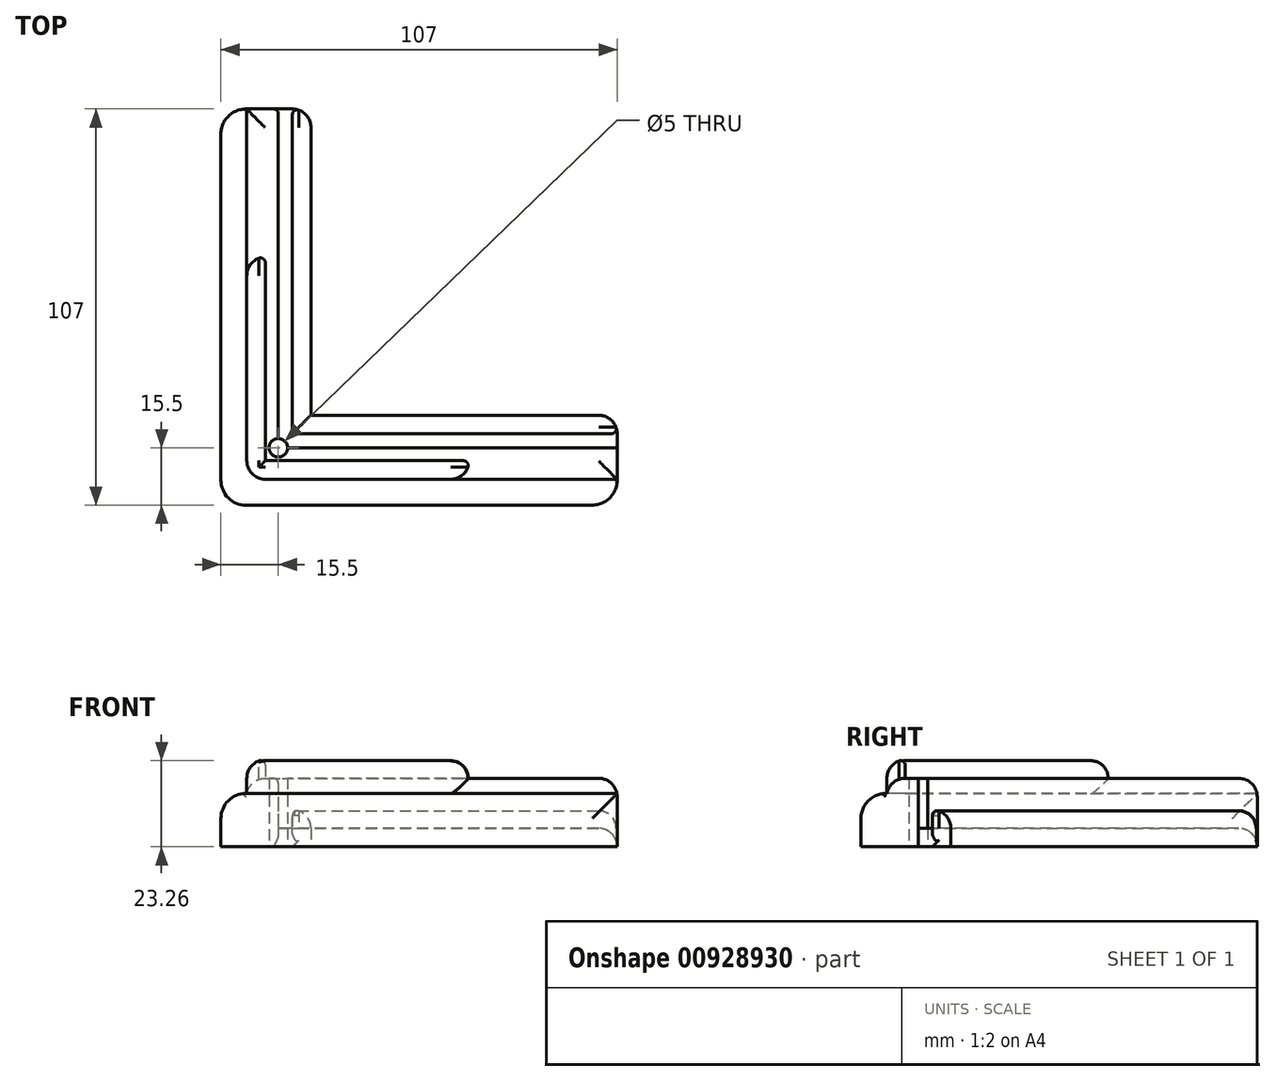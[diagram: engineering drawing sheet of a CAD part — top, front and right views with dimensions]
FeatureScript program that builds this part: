
annotation { "Feature Type Name" : "Feature", "Feature Type Description" : "" }
export const myFeature = defineFeature(function(context is Context, id is Id, definition is map)
    precondition{}
    {
        {
            var Q0;
            Q0=qCreatedBy(makeId("Top.planeOp"),FACE);
            var sketch = newSketch(context, id + "F0", { "sketchPlane" : qUnion([Q0])});
            skLineSegment(sketch, "E0", {"start": v(0, 0) * mm, "end": v(0, 91.5) * mm});
            skLineSegment(sketch, "E1", {"start": v(0, 91.5) * mm, "end": v(3.8, 91.5) * mm});
            skLineSegment(sketch, "E2", {"start": v(3.8, 91.5) * mm, "end": v(3.8, 3.8) * mm});
            skLineSegment(sketch, "E3", {"start": v(3.8, 3.8) * mm, "end": v(91.5, 3.8) * mm});
            skLineSegment(sketch, "E4", {"start": v(91.5, 3.8) * mm, "end": v(91.5, 0) * mm});
            skLineSegment(sketch, "E5", {"start": v(91.5, 0) * mm, "end": v(0, 0) * mm});
            skLineSegment(sketch, "E6", {"start": v(3.8, 91.5) * mm, "end": v(8.8, 91.5) * mm});
            skLineSegment(sketch, "E7", {"start": v(8.8, 91.5) * mm, "end": v(8.8, 8.8) * mm});
            skLineSegment(sketch, "E8", {"start": v(8.8, 8.8) * mm, "end": v(91.5, 8.8) * mm});
            skLineSegment(sketch, "E9", {"start": v(91.5, 8.8) * mm, "end": v(91.5, 3.8) * mm});
            skLineSegment(sketch, "E10", {"start": v(91.5, 0) * mm, "end": v(91.5, -3.5) * mm});
            skLineSegment(sketch, "E11", {"start": v(-3.5, 91.5) * mm, "end": v(0, 91.5) * mm});
            skLineSegment(sketch, "E12", {"start": v(91.5, -3.5) * mm, "end": v(91.5, -8.5) * mm});
            skLineSegment(sketch, "E13", {"start": v(91.5, -8.5) * mm, "end": v(-8.5, -8.5) * mm});
            skLineSegment(sketch, "E14", {"start": v(-8.5, -8.5) * mm, "end": v(-8.5, 91.5) * mm});
            skLineSegment(sketch, "E15", {"start": v(-8.5, 91.5) * mm, "end": v(-3.5, 91.5) * mm});
            skLineSegment(sketch, "E16", {"start": v(-8.5, 91.5) * mm, "end": v(-15.5, 91.5) * mm});
            skLineSegment(sketch, "E17", {"start": v(-15.5, 91.5) * mm, "end": v(-15.5, -15.5) * mm});
            skLineSegment(sketch, "E18", {"start": v(-15.5, -15.5) * mm, "end": v(91.5, -15.5) * mm});
            skLineSegment(sketch, "E19", {"start": v(91.5, -15.5) * mm, "end": v(91.5, -8.5) * mm});
            skSolve(sketch);
        }
        {
            var Q0;
            Q0=makeQuery(id+"F0.imprint","IMPRINT",FACE,{"disambiguationData":[TD([[makeQuery(id+"F0.imprint","IMPRINT",EDGE,{"derivedFrom":sQuery(id+"F0.wireOp",EDGE,"E2")}),1.0]])]});
            var Q1;
            Q1=makeQuery(id+"F0.imprint","IMPRINT",FACE,{"disambiguationData":[TD([[makeQuery(id+"F0.imprint","IMPRINT",EDGE,{"derivedFrom":sQuery(id+"F0.wireOp",EDGE,"E0")}),-1.0]])]});
            var Q2;
            Q2=makeQuery(id+"F0.imprint","IMPRINT",FACE,{"disambiguationData":[TD([[makeQuery(id+"F0.imprint","IMPRINT",EDGE,{"derivedFrom":sQuery(id+"F0.wireOp",EDGE,"E0")}),1.0]])]});
            var Q3;
            Q3=makeQuery(id+"F0.imprint","IMPRINT",FACE,{"disambiguationData":[TD([[makeQuery(id+"F0.imprint","IMPRINT",EDGE,{"derivedFrom":sQuery(id+"F0.wireOp",EDGE,"OfsXpkOs-3l8G-isar-b0VL-Z3l6h46DC14G")}),1.0]])]});
            extrude(context, id + "F1", {"entities" : qUnion([Q0, Q1, Q2, Q3]), "depth" : 5 * mm, "offsetDistance" : 25 * mm});
        }
        {
            var Q0;
            Q0=makeQuery(id+"F1.opExtrude","CAP_FACE",FACE,{"disambiguationData":[OSD([sQuery(id+"F0.wireOp",EDGE,"E1"),sQuery(id+"F0.wireOp",EDGE,"E4"),sQuery(id+"F0.wireOp",EDGE,"E6"),sQuery(id+"F0.wireOp",EDGE,"E7"),sQuery(id+"F0.wireOp",EDGE,"E8"),sQuery(id+"F0.wireOp",EDGE,"E9"),sQuery(id+"F0.wireOp",EDGE,"E10"),sQuery(id+"F0.wireOp",EDGE,"E11"),sQuery(id+"F0.wireOp",EDGE,"E12"),sQuery(id+"F0.wireOp",EDGE,"E13"),sQuery(id+"F0.wireOp",EDGE,"E14"),sQuery(id+"F0.wireOp",EDGE,"E15")])],"isStart":false});
            var sketch = newSketch(context, id + "F2", { "sketchPlane" : qUnion([Q0])});
            skLineSegment(sketch, "E20", {"start": v(0, 0) * mm, "end": v(0, 91.5) * mm});
            skLineSegment(sketch, "E21", {"start": v(0, 91.5) * mm, "end": v(3.8, 91.5) * mm});
            skLineSegment(sketch, "E22", {"start": v(3.8, 91.5) * mm, "end": v(3.8, 3.8) * mm});
            skLineSegment(sketch, "E23", {"start": v(3.8, 3.8) * mm, "end": v(91.5, 3.8) * mm});
            skLineSegment(sketch, "E24", {"start": v(91.5, 3.8) * mm, "end": v(91.5, 0) * mm});
            skLineSegment(sketch, "E25", {"start": v(91.5, 0) * mm, "end": v(0, 0) * mm});
            skLineSegment(sketch, "E26", {"start": v(3.8, 91.5) * mm, "end": v(8.8, 91.5) * mm});
            skLineSegment(sketch, "E27", {"start": v(8.8, 91.5) * mm, "end": v(8.8, 8.8) * mm});
            skLineSegment(sketch, "E28", {"start": v(8.8, 8.8) * mm, "end": v(91.5, 8.8) * mm});
            skLineSegment(sketch, "E29", {"start": v(91.5, 8.8) * mm, "end": v(91.5, 3.8) * mm});
            skLineSegment(sketch, "E30", {"start": v(91.5, 0) * mm, "end": v(91.5, -3.5) * mm});
            skLineSegment(sketch, "E31", {"start": v(-3.5, -3.5) * mm, "end": v(-3.5, 91.5) * mm});
            skLineSegment(sketch, "E32", {"start": v(-3.5, 91.5) * mm, "end": v(0, 91.5) * mm});
            skLineSegment(sketch, "E33", {"start": v(91.5, -3.5) * mm, "end": v(91.5, -8.5) * mm});
            skLineSegment(sketch, "E34", {"start": v(91.5, -8.5) * mm, "end": v(-8.5, -8.5) * mm});
            skLineSegment(sketch, "E35", {"start": v(-8.5, -8.5) * mm, "end": v(-8.5, 91.5) * mm});
            skLineSegment(sketch, "E36", {"start": v(-8.5, 91.5) * mm, "end": v(-3.5, 91.5) * mm});
            skLineSegment(sketch, "E37", {"start": v(-3.5, -3.5) * mm, "end": v(91.5, -3.5) * mm});
            skSolve(sketch);
        }
        {
            var Q0;
            Q0=makeQuery(id+"F2.imprint","IMPRINT",FACE,{"disambiguationData":[TD([[makeQuery(id+"F2.imprint","IMPRINT",EDGE,{"derivedFrom":sQuery(id+"F2.wireOp",EDGE,"E22")}),1.0]])]});
            var Q1;
            Q1=makeQuery(id+"F2.imprint","IMPRINT",FACE,{"disambiguationData":[TD([[makeQuery(id+"F2.imprint","IMPRINT",EDGE,{"derivedFrom":sQuery(id+"F2.wireOp",EDGE,"E20")}),1.0]])]});
            var Q2;
            Q2=makeQuery(id+"F2.imprint","IMPRINT",FACE,{"disambiguationData":[TD([[makeQuery(id+"F2.imprint","IMPRINT",EDGE,{"derivedFrom":sQuery(id+"F2.wireOp",EDGE,"E31")}),1.0]])]});
            extrude(context, id + "F3", {"entities" : qUnion([Q0, Q1, Q2]), "operationType" : NewBodyOperationType.ADD, "depth" : 5 * mm, "offsetDistance" : 25 * mm});
        }
        {
            var Q0;
            Q0=makeQuery(id+"F3.opExtrude","CAP_FACE",FACE,{"disambiguationData":[OSD([sQuery(id+"F2.wireOp",EDGE,"E20"),sQuery(id+"F2.wireOp",EDGE,"E25"),sQuery(id+"F2.wireOp",EDGE,"E30"),sQuery(id+"F2.wireOp",EDGE,"E32"),sQuery(id+"F2.wireOp",EDGE,"E33"),sQuery(id+"F2.wireOp",EDGE,"E34"),sQuery(id+"F2.wireOp",EDGE,"E35"),sQuery(id+"F2.wireOp",EDGE,"E36")])],"isStart":false});
            var sketch = newSketch(context, id + "F4", { "sketchPlane" : qUnion([Q0])});
            skLineSegment(sketch, "E38", {"start": v(0, 0) * mm, "end": v(0, 91.5) * mm});
            skLineSegment(sketch, "E39", {"start": v(0, 91.5) * mm, "end": v(3.8, 91.5) * mm});
            skLineSegment(sketch, "E40", {"start": v(3.8, 91.5) * mm, "end": v(3.8, 3.8) * mm});
            skLineSegment(sketch, "E41", {"start": v(3.8, 3.8) * mm, "end": v(91.5, 3.8) * mm});
            skLineSegment(sketch, "E42", {"start": v(91.5, 3.8) * mm, "end": v(91.5, 0) * mm});
            skLineSegment(sketch, "E43", {"start": v(91.5, 0) * mm, "end": v(0, 0) * mm});
            skLineSegment(sketch, "E44", {"start": v(3.8, 91.5) * mm, "end": v(8.8, 91.5) * mm});
            skLineSegment(sketch, "E45", {"start": v(8.8, 91.5) * mm, "end": v(8.8, 8.8) * mm});
            skLineSegment(sketch, "E46", {"start": v(8.8, 8.8) * mm, "end": v(91.5, 8.8) * mm});
            skLineSegment(sketch, "E47", {"start": v(91.5, 8.8) * mm, "end": v(91.5, 3.8) * mm});
            skLineSegment(sketch, "E48", {"start": v(91.5, 0) * mm, "end": v(91.5, -3.5) * mm});
            skLineSegment(sketch, "E49", {"start": v(-3.5, -3.5) * mm, "end": v(-3.5, 91.5) * mm});
            skLineSegment(sketch, "E50", {"start": v(-3.5, 91.5) * mm, "end": v(0, 91.5) * mm});
            skLineSegment(sketch, "E51", {"start": v(91.5, -3.5) * mm, "end": v(91.5, -8.5) * mm});
            skLineSegment(sketch, "E52", {"start": v(91.5, -8.5) * mm, "end": v(-8.5, -8.5) * mm});
            skLineSegment(sketch, "E53", {"start": v(-8.5, -8.5) * mm, "end": v(-8.5, 91.5) * mm});
            skLineSegment(sketch, "E54", {"start": v(-8.5, 91.5) * mm, "end": v(-3.5, 91.5) * mm});
            skLineSegment(sketch, "E55", {"start": v(-3.5, -3.5) * mm, "end": v(91.5, -3.5) * mm});
            skSolve(sketch);
        }
        {
            var Q0;
            Q0=makeQuery(id+"F4.imprint","IMPRINT",FACE,{"disambiguationData":[TD([[makeQuery(id+"F4.imprint","IMPRINT",EDGE,{"derivedFrom":sQuery(id+"F4.wireOp",EDGE,"E38")}),1.0]])]});
            var Q1;
            Q1=makeQuery(id+"F4.imprint","IMPRINT",FACE,{"disambiguationData":[TD([[makeQuery(id+"F4.imprint","IMPRINT",EDGE,{"derivedFrom":sQuery(id+"F4.wireOp",EDGE,"E49")}),1.0]])]});
            extrude(context, id + "F5", {"entities" : qUnion([Q0, Q1]), "operationType" : NewBodyOperationType.ADD, "depth" : 8.5 * mm, "offsetDistance" : 25 * mm});
        }
        {
            var Q0;
            Q0=makeQuery(id+"F5.opExtrude","CAP_FACE",FACE,{"disambiguationData":[OSD([sQuery(id+"F4.wireOp",EDGE,"E38"),sQuery(id+"F4.wireOp",EDGE,"E43"),sQuery(id+"F4.wireOp",EDGE,"E48"),sQuery(id+"F4.wireOp",EDGE,"E50"),sQuery(id+"F4.wireOp",EDGE,"E51"),sQuery(id+"F4.wireOp",EDGE,"E52"),sQuery(id+"F4.wireOp",EDGE,"E53"),sQuery(id+"F4.wireOp",EDGE,"E54")])],"isStart":false});
            var sketch = newSketch(context, id + "F6", { "sketchPlane" : qUnion([Q0])});
            skLineSegment(sketch, "E56", {"start": v(0, 0) * mm, "end": v(0, 51.5) * mm});
            skLineSegment(sketch, "E57", {"start": v(0, 51.5) * mm, "end": v(3.8, 51.5) * mm});
            skLineSegment(sketch, "E58", {"start": v(3.8, 51.5) * mm, "end": v(3.8, 3.8) * mm});
            skLineSegment(sketch, "E59", {"start": v(3.8, 3.8) * mm, "end": v(51.5, 3.8) * mm});
            skLineSegment(sketch, "E60", {"start": v(51.5, 3.8) * mm, "end": v(51.5, 0) * mm});
            skLineSegment(sketch, "E61", {"start": v(51.5, 0) * mm, "end": v(0, 0) * mm});
            skLineSegment(sketch, "E62", {"start": v(3.8, 51.5) * mm, "end": v(8.8, 51.5) * mm});
            skLineSegment(sketch, "E63", {"start": v(8.8, 51.5) * mm, "end": v(8.8, 8.8) * mm});
            skLineSegment(sketch, "E64", {"start": v(8.8, 8.8) * mm, "end": v(51.5, 8.8) * mm});
            skLineSegment(sketch, "E65", {"start": v(51.5, 8.8) * mm, "end": v(51.5, 3.8) * mm});
            skLineSegment(sketch, "E66", {"start": v(51.5, 0) * mm, "end": v(51.5, -3.5) * mm});
            skLineSegment(sketch, "E67", {"start": v(-3.5, -3.5) * mm, "end": v(-3.5, 51.5) * mm});
            skLineSegment(sketch, "E68", {"start": v(-3.5, 51.5) * mm, "end": v(0, 51.5) * mm});
            skLineSegment(sketch, "E69", {"start": v(51.5, -3.5) * mm, "end": v(51.5, -8.5) * mm});
            skLineSegment(sketch, "E70", {"start": v(51.5, -8.5) * mm, "end": v(-8.5, -8.5) * mm});
            skLineSegment(sketch, "E71", {"start": v(-8.5, -8.5) * mm, "end": v(-8.5, 51.5) * mm});
            skLineSegment(sketch, "E72", {"start": v(-8.5, 51.5) * mm, "end": v(-3.5, 51.5) * mm});
            skLineSegment(sketch, "E73", {"start": v(-3.5, -3.5) * mm, "end": v(51.5, -3.5) * mm});
            skSolve(sketch);
        }
        {
            var Q0;
            Q0=makeQuery(id+"F6.imprint","IMPRINT",FACE,{"disambiguationData":[TD([[makeQuery(id+"F6.imprint","IMPRINT",EDGE,{"derivedFrom":sQuery(id+"F6.wireOp",EDGE,"E67")}),1.0]])]});
            extrude(context, id + "F7", {"entities" : qUnion([Q0]), "operationType" : NewBodyOperationType.ADD, "depth" : 5 * mm, "offsetDistance" : 25 * mm});
        }
        {
            var Q0;
            Q0=makeQuery(id+"F0.imprint","IMPRINT",FACE,{"disambiguationData":[TD([[makeQuery(id+"F0.imprint","IMPRINT",EDGE,{"derivedFrom":sQuery(id+"F0.wireOp",EDGE,"E13")}),1.0]])]});
            extrude(context, id + "F8", {"entities" : qUnion([Q0]), "operationType" : NewBodyOperationType.ADD, "depth" : 14.4 * mm, "offsetDistance" : 25 * mm});
        }
        {
            var Q0;
            Q0=makeQuery(id+"F8.opExtrude","CAP_EDGE",EDGE,{"disambiguationData":[OSD([sQuery(id+"F0.wireOp",EDGE,"E18")])],"isStart":false});
            var Q1;
            Q1=makeQuery(id+"F8.opExtrude","CAP_EDGE",EDGE,{"disambiguationData":[OSD([sQuery(id+"F0.wireOp",EDGE,"E17")])],"isStart":false});
            var Q2;
            Q2=makeQuery(id+"F8.opExtrude","SWEPT_EDGE",EDGE,{"disambiguationData":[OSD([sQuery(id+"F0.wireOp",EDGE,"E17"),sQuery(id+"F0.wireOp",EDGE,"E18")])]});
            var Q3;
            Q3=makeQuery(id+"F8.opExtrude","SWEPT_EDGE",EDGE,{"disambiguationData":[OSD([sQuery(id+"F0.wireOp",EDGE,"E18"),sQuery(id+"F0.wireOp",EDGE,"E19")])]});
            var Q4;
            Q4=makeQuery(id+"F8.opExtrude","SWEPT_EDGE",EDGE,{"disambiguationData":[OSD([sQuery(id+"F0.wireOp",EDGE,"E16"),sQuery(id+"F0.wireOp",EDGE,"E17")])]});
            fillet(context, id + "F9", {"entities" : qUnion([Q0, Q1, Q2, Q3, Q4]), "radius" : 6.76 * mm, "tangentPropagation" : true, "allowEdgeOverflow" : false});
        }
        {
            var Q0;
            Q0=qCreatedBy(makeId("Top.planeOp"),FACE);
            var sketch = newSketch(context, id + "F10", { "sketchPlane" : qUnion([Q0])});
            skPoint(sketch, "E74", {"position": v(0, 0) * mm});
            skSolve(sketch);
        }
        {
            var Q0;
            Q0=sQuery(id+"F10.wireOp",VERTEX,"E74");
            var Q1;
            Q1=makeQuery(id+"F1.opExtrude","SWEPT_BODY",BODY,{"disambiguationData":[OSD([sQuery(id+"F0.wireOp",EDGE,"E1"),sQuery(id+"F0.wireOp",EDGE,"E4"),sQuery(id+"F0.wireOp",EDGE,"E6"),sQuery(id+"F0.wireOp",EDGE,"E7"),sQuery(id+"F0.wireOp",EDGE,"E8"),sQuery(id+"F0.wireOp",EDGE,"E9"),sQuery(id+"F0.wireOp",EDGE,"E10"),sQuery(id+"F0.wireOp",EDGE,"E11"),sQuery(id+"F0.wireOp",EDGE,"E12"),sQuery(id+"F0.wireOp",EDGE,"E13"),sQuery(id+"F0.wireOp",EDGE,"E14"),sQuery(id+"F0.wireOp",EDGE,"E15")])]});
            hole(context, id + "F11", {"style" : HoleStyle.SIMPLE, "endStyle" : HoleEndStyle.THROUGH, "oppositeDirection" : true, "holeDiameter" : 5 * mm, "majorDiameter" : 5 * mm, "isTappedThrough" : true, "tappedDepth" : 12 * mm, "tapClearance" : 3, "locations" : qUnion([Q0]), "scope" : qUnion([Q1])});
        }
        {
            var Q0;
            Q0=makeQuery(id+"F11.hole-0.boolean.opBoolean","INTERSECT",EDGE,{"derivedFrom":[makeQuery(id+"F5.boolean.opBoolean","MERGE",FACE,{"derivedFrom":[makeQuery(id+"F3.opExtrude","SWEPT_FACE",FACE,{"disambiguationData":[OSD([sQuery(id+"F2.wireOp",EDGE,"E20")])]}),makeQuery(id+"F5.opExtrude","SWEPT_FACE",FACE,{"disambiguationData":[OSD([sQuery(id+"F4.wireOp",EDGE,"E38")])]})]}),makeQuery(id+"F11.hole-0.opRevolve","SWEPT_FACE",FACE,{"disambiguationData":[OSD([sQuery(id+"F11.hole-0.sketch.wireOp",EDGE,"core_line_2")])]})]});
            var Q1;
            Q1=makeQuery(id+"F11.hole-0.boolean.opBoolean","INTERSECT",EDGE,{"derivedFrom":[makeQuery(id+"F5.boolean.opBoolean","MERGE",FACE,{"derivedFrom":[makeQuery(id+"F3.opExtrude","SWEPT_FACE",FACE,{"disambiguationData":[OSD([sQuery(id+"F2.wireOp",EDGE,"E25")])]}),makeQuery(id+"F5.opExtrude","SWEPT_FACE",FACE,{"disambiguationData":[OSD([sQuery(id+"F4.wireOp",EDGE,"E43")])]})]}),makeQuery(id+"F11.hole-0.opRevolve","SWEPT_FACE",FACE,{"disambiguationData":[OSD([sQuery(id+"F11.hole-0.sketch.wireOp",EDGE,"core_line_2")])]})]});
            var Q2;
            Q2=makeQuery(id+"F3.opExtrude","SWEPT_EDGE",EDGE,{"disambiguationData":[OSD([sQuery(id+"F2.wireOp",EDGE,"E22"),sQuery(id+"F2.wireOp",EDGE,"E23")])]});
            fillet(context, id + "F12", {"entities" : qUnion([Q0, Q1, Q2]), "radius" : 1.42 * mm, "tangentPropagation" : true, "allowEdgeOverflow" : false});
        }
        {
            var Q0;
            Q0=makeQuery(id+"F7.opExtrude","CAP_EDGE",EDGE,{"disambiguationData":[OSD([sQuery(id+"F6.wireOp",EDGE,"E70")])],"isStart":false});
            var Q1;
            Q1=makeQuery(id+"F5.opExtrude","CAP_EDGE",EDGE,{"disambiguationData":[OSD([sQuery(id+"F4.wireOp",EDGE,"E52")])],"isStart":false});
            var Q2;
            Q2=makeQuery(id+"F7.opExtrude","CAP_EDGE",EDGE,{"disambiguationData":[OSD([sQuery(id+"F6.wireOp",EDGE,"E71")])],"isStart":false});
            var Q3;
            Q3=makeQuery(id+"F5.opExtrude","CAP_EDGE",EDGE,{"disambiguationData":[OSD([sQuery(id+"F4.wireOp",EDGE,"E53")])],"isStart":false});
            var Q4;
            Q4=makeQuery(id+"F3.opExtrude","CAP_EDGE",EDGE,{"disambiguationData":[OSD([sQuery(id+"F2.wireOp",EDGE,"E27")])],"isStart":false});
            var Q5;
            Q5=makeQuery(id+"F3.opExtrude","CAP_EDGE",EDGE,{"disambiguationData":[OSD([sQuery(id+"F2.wireOp",EDGE,"E28")])],"isStart":false});
            var Q6;
            Q6=makeQuery(id+"F1.opExtrude","CAP_EDGE",EDGE,{"disambiguationData":[OSD([sQuery(id+"F0.wireOp",EDGE,"E1"),sQuery(id+"F0.wireOp",EDGE,"E6"),sQuery(id+"F0.wireOp",EDGE,"E11"),sQuery(id+"F0.wireOp",EDGE,"E15")])],"isStart":false});
            var Q7;
            Q7=makeQuery(id+"F1.opExtrude","CAP_EDGE",EDGE,{"disambiguationData":[OSD([sQuery(id+"F0.wireOp",EDGE,"E4"),sQuery(id+"F0.wireOp",EDGE,"E9"),sQuery(id+"F0.wireOp",EDGE,"E10"),sQuery(id+"F0.wireOp",EDGE,"E12")])],"isStart":false});
            fillet(context, id + "F13", {"entities" : qUnion([Q0, Q1, Q2, Q3, Q4, Q5, Q6, Q7]), "radius" : 5 * mm, "tangentPropagation" : true, "allowEdgeOverflow" : false});
        }
        {
            var Q0;
            Q0=makeQuery(id+"F13.opFillet","BLEND_EDGE",EDGE,{"blendedFrom":[makeQuery(id+"F7.opExtrude","CAP_EDGE",EDGE,{"disambiguationData":[OSD([sQuery(id+"F6.wireOp",EDGE,"E70")])],"isStart":false}),makeQuery(id+"F7.opExtrude","SWEPT_FACE",FACE,{"disambiguationData":[OSD([sQuery(id+"F6.wireOp",EDGE,"E69")])]})],"blendedInto":[makeQuery(id+"F7.opExtrude","SWEPT_FACE",FACE,{"disambiguationData":[OSD([sQuery(id+"F6.wireOp",EDGE,"E69")])]})]});
            var Q1;
            Q1=makeQuery(id+"F13.opFillet","BLEND_EDGE",EDGE,{"blendedFrom":[makeQuery(id+"F7.opExtrude","CAP_EDGE",EDGE,{"disambiguationData":[OSD([sQuery(id+"F6.wireOp",EDGE,"E71")])],"isStart":false}),makeQuery(id+"F7.opExtrude","SWEPT_FACE",FACE,{"disambiguationData":[OSD([sQuery(id+"F6.wireOp",EDGE,"E72")])]})],"blendedInto":[makeQuery(id+"F7.opExtrude","SWEPT_FACE",FACE,{"disambiguationData":[OSD([sQuery(id+"F6.wireOp",EDGE,"E72")])]})]});
            var Q2;
            Q2=makeQuery(id+"F13.opFillet","BLEND_EDGE",EDGE,{"blendedFrom":[makeQuery(id+"F5.opExtrude","CAP_EDGE",EDGE,{"disambiguationData":[OSD([sQuery(id+"F4.wireOp",EDGE,"E53")])],"isStart":false}),makeQuery(id+"F8.boolean.opBoolean","MERGE",FACE,{"derivedFrom":[makeQuery(id+"F5.boolean.opBoolean","MERGE",FACE,{"derivedFrom":[makeQuery(id+"F3.boolean.opBoolean","MERGE",FACE,{"derivedFrom":[makeQuery(id+"F1.opExtrude","SWEPT_FACE",FACE,{"disambiguationData":[OSD([sQuery(id+"F0.wireOp",EDGE,"E1"),sQuery(id+"F0.wireOp",EDGE,"E6"),sQuery(id+"F0.wireOp",EDGE,"E11"),sQuery(id+"F0.wireOp",EDGE,"E15")])]}),makeQuery(id+"F3.opExtrude","SWEPT_FACE",FACE,{"disambiguationData":[OSD([sQuery(id+"F2.wireOp",EDGE,"E26")])]}),makeQuery(id+"F3.opExtrude","SWEPT_FACE",FACE,{"disambiguationData":[OSD([sQuery(id+"F2.wireOp",EDGE,"E32"),sQuery(id+"F2.wireOp",EDGE,"E36")])]})]}),makeQuery(id+"F5.opExtrude","SWEPT_FACE",FACE,{"disambiguationData":[OSD([sQuery(id+"F4.wireOp",EDGE,"E50"),sQuery(id+"F4.wireOp",EDGE,"E54")])]})]}),makeQuery(id+"F8.opExtrude","SWEPT_FACE",FACE,{"disambiguationData":[OSD([sQuery(id+"F0.wireOp",EDGE,"E16")])]})]})],"blendedInto":[makeQuery(id+"F8.boolean.opBoolean","MERGE",FACE,{"derivedFrom":[makeQuery(id+"F5.boolean.opBoolean","MERGE",FACE,{"derivedFrom":[makeQuery(id+"F3.boolean.opBoolean","MERGE",FACE,{"derivedFrom":[makeQuery(id+"F1.opExtrude","SWEPT_FACE",FACE,{"disambiguationData":[OSD([sQuery(id+"F0.wireOp",EDGE,"E1"),sQuery(id+"F0.wireOp",EDGE,"E6"),sQuery(id+"F0.wireOp",EDGE,"E11"),sQuery(id+"F0.wireOp",EDGE,"E15")])]}),makeQuery(id+"F3.opExtrude","SWEPT_FACE",FACE,{"disambiguationData":[OSD([sQuery(id+"F2.wireOp",EDGE,"E26")])]}),makeQuery(id+"F3.opExtrude","SWEPT_FACE",FACE,{"disambiguationData":[OSD([sQuery(id+"F2.wireOp",EDGE,"E32"),sQuery(id+"F2.wireOp",EDGE,"E36")])]})]}),makeQuery(id+"F5.opExtrude","SWEPT_FACE",FACE,{"disambiguationData":[OSD([sQuery(id+"F4.wireOp",EDGE,"E50"),sQuery(id+"F4.wireOp",EDGE,"E54")])]})]}),makeQuery(id+"F8.opExtrude","SWEPT_FACE",FACE,{"disambiguationData":[OSD([sQuery(id+"F0.wireOp",EDGE,"E16")])]})]})]});
            var Q3;
            Q3=makeQuery(id+"F13.opFillet","BLEND_EDGE",EDGE,{"blendedFrom":[makeQuery(id+"F5.opExtrude","CAP_EDGE",EDGE,{"disambiguationData":[OSD([sQuery(id+"F4.wireOp",EDGE,"E52")])],"isStart":false}),makeQuery(id+"F8.boolean.opBoolean","MERGE",FACE,{"derivedFrom":[makeQuery(id+"F5.boolean.opBoolean","MERGE",FACE,{"derivedFrom":[makeQuery(id+"F3.boolean.opBoolean","MERGE",FACE,{"derivedFrom":[makeQuery(id+"F1.opExtrude","SWEPT_FACE",FACE,{"disambiguationData":[OSD([sQuery(id+"F0.wireOp",EDGE,"E4"),sQuery(id+"F0.wireOp",EDGE,"E9"),sQuery(id+"F0.wireOp",EDGE,"E10"),sQuery(id+"F0.wireOp",EDGE,"E12")])]}),makeQuery(id+"F3.opExtrude","SWEPT_FACE",FACE,{"disambiguationData":[OSD([sQuery(id+"F2.wireOp",EDGE,"E29")])]}),makeQuery(id+"F3.opExtrude","SWEPT_FACE",FACE,{"disambiguationData":[OSD([sQuery(id+"F2.wireOp",EDGE,"E30"),sQuery(id+"F2.wireOp",EDGE,"E33")])]})]}),makeQuery(id+"F5.opExtrude","SWEPT_FACE",FACE,{"disambiguationData":[OSD([sQuery(id+"F4.wireOp",EDGE,"E48"),sQuery(id+"F4.wireOp",EDGE,"E51")])]})]}),makeQuery(id+"F8.opExtrude","SWEPT_FACE",FACE,{"disambiguationData":[OSD([sQuery(id+"F0.wireOp",EDGE,"E19")])]})]})],"blendedInto":[makeQuery(id+"F8.boolean.opBoolean","MERGE",FACE,{"derivedFrom":[makeQuery(id+"F5.boolean.opBoolean","MERGE",FACE,{"derivedFrom":[makeQuery(id+"F3.boolean.opBoolean","MERGE",FACE,{"derivedFrom":[makeQuery(id+"F1.opExtrude","SWEPT_FACE",FACE,{"disambiguationData":[OSD([sQuery(id+"F0.wireOp",EDGE,"E4"),sQuery(id+"F0.wireOp",EDGE,"E9"),sQuery(id+"F0.wireOp",EDGE,"E10"),sQuery(id+"F0.wireOp",EDGE,"E12")])]}),makeQuery(id+"F3.opExtrude","SWEPT_FACE",FACE,{"disambiguationData":[OSD([sQuery(id+"F2.wireOp",EDGE,"E29")])]}),makeQuery(id+"F3.opExtrude","SWEPT_FACE",FACE,{"disambiguationData":[OSD([sQuery(id+"F2.wireOp",EDGE,"E30"),sQuery(id+"F2.wireOp",EDGE,"E33")])]})]}),makeQuery(id+"F5.opExtrude","SWEPT_FACE",FACE,{"disambiguationData":[OSD([sQuery(id+"F4.wireOp",EDGE,"E48"),sQuery(id+"F4.wireOp",EDGE,"E51")])]})]}),makeQuery(id+"F8.opExtrude","SWEPT_FACE",FACE,{"disambiguationData":[OSD([sQuery(id+"F0.wireOp",EDGE,"E19")])]})]})]});
            var Q4;
            Q4=makeQuery(id+"F13.opFillet","BLEND_EDGE",EDGE,{"blendedFrom":[makeQuery(id+"F3.opExtrude","CAP_EDGE",EDGE,{"disambiguationData":[OSD([sQuery(id+"F2.wireOp",EDGE,"E28")])],"isStart":false}),makeQuery(id+"F8.boolean.opBoolean","MERGE",FACE,{"derivedFrom":[makeQuery(id+"F5.boolean.opBoolean","MERGE",FACE,{"derivedFrom":[makeQuery(id+"F3.boolean.opBoolean","MERGE",FACE,{"derivedFrom":[makeQuery(id+"F1.opExtrude","SWEPT_FACE",FACE,{"disambiguationData":[OSD([sQuery(id+"F0.wireOp",EDGE,"E4"),sQuery(id+"F0.wireOp",EDGE,"E9"),sQuery(id+"F0.wireOp",EDGE,"E10"),sQuery(id+"F0.wireOp",EDGE,"E12")])]}),makeQuery(id+"F3.opExtrude","SWEPT_FACE",FACE,{"disambiguationData":[OSD([sQuery(id+"F2.wireOp",EDGE,"E29")])]}),makeQuery(id+"F3.opExtrude","SWEPT_FACE",FACE,{"disambiguationData":[OSD([sQuery(id+"F2.wireOp",EDGE,"E30"),sQuery(id+"F2.wireOp",EDGE,"E33")])]})]}),makeQuery(id+"F5.opExtrude","SWEPT_FACE",FACE,{"disambiguationData":[OSD([sQuery(id+"F4.wireOp",EDGE,"E48"),sQuery(id+"F4.wireOp",EDGE,"E51")])]})]}),makeQuery(id+"F8.opExtrude","SWEPT_FACE",FACE,{"disambiguationData":[OSD([sQuery(id+"F0.wireOp",EDGE,"E19")])]})]})],"blendedInto":[makeQuery(id+"F8.boolean.opBoolean","MERGE",FACE,{"derivedFrom":[makeQuery(id+"F5.boolean.opBoolean","MERGE",FACE,{"derivedFrom":[makeQuery(id+"F3.boolean.opBoolean","MERGE",FACE,{"derivedFrom":[makeQuery(id+"F1.opExtrude","SWEPT_FACE",FACE,{"disambiguationData":[OSD([sQuery(id+"F0.wireOp",EDGE,"E4"),sQuery(id+"F0.wireOp",EDGE,"E9"),sQuery(id+"F0.wireOp",EDGE,"E10"),sQuery(id+"F0.wireOp",EDGE,"E12")])]}),makeQuery(id+"F3.opExtrude","SWEPT_FACE",FACE,{"disambiguationData":[OSD([sQuery(id+"F2.wireOp",EDGE,"E29")])]}),makeQuery(id+"F3.opExtrude","SWEPT_FACE",FACE,{"disambiguationData":[OSD([sQuery(id+"F2.wireOp",EDGE,"E30"),sQuery(id+"F2.wireOp",EDGE,"E33")])]})]}),makeQuery(id+"F5.opExtrude","SWEPT_FACE",FACE,{"disambiguationData":[OSD([sQuery(id+"F4.wireOp",EDGE,"E48"),sQuery(id+"F4.wireOp",EDGE,"E51")])]})]}),makeQuery(id+"F8.opExtrude","SWEPT_FACE",FACE,{"disambiguationData":[OSD([sQuery(id+"F0.wireOp",EDGE,"E19")])]})]})]});
            var Q5;
            Q5=makeQuery(id+"F13.opFillet","BLEND_EDGE",EDGE,{"blendedFrom":[makeQuery(id+"F3.opExtrude","CAP_EDGE",EDGE,{"disambiguationData":[OSD([sQuery(id+"F2.wireOp",EDGE,"E27")])],"isStart":false}),makeQuery(id+"F8.boolean.opBoolean","MERGE",FACE,{"derivedFrom":[makeQuery(id+"F5.boolean.opBoolean","MERGE",FACE,{"derivedFrom":[makeQuery(id+"F3.boolean.opBoolean","MERGE",FACE,{"derivedFrom":[makeQuery(id+"F1.opExtrude","SWEPT_FACE",FACE,{"disambiguationData":[OSD([sQuery(id+"F0.wireOp",EDGE,"E1"),sQuery(id+"F0.wireOp",EDGE,"E6"),sQuery(id+"F0.wireOp",EDGE,"E11"),sQuery(id+"F0.wireOp",EDGE,"E15")])]}),makeQuery(id+"F3.opExtrude","SWEPT_FACE",FACE,{"disambiguationData":[OSD([sQuery(id+"F2.wireOp",EDGE,"E26")])]}),makeQuery(id+"F3.opExtrude","SWEPT_FACE",FACE,{"disambiguationData":[OSD([sQuery(id+"F2.wireOp",EDGE,"E32"),sQuery(id+"F2.wireOp",EDGE,"E36")])]})]}),makeQuery(id+"F5.opExtrude","SWEPT_FACE",FACE,{"disambiguationData":[OSD([sQuery(id+"F4.wireOp",EDGE,"E50"),sQuery(id+"F4.wireOp",EDGE,"E54")])]})]}),makeQuery(id+"F8.opExtrude","SWEPT_FACE",FACE,{"disambiguationData":[OSD([sQuery(id+"F0.wireOp",EDGE,"E16")])]})]})],"blendedInto":[makeQuery(id+"F8.boolean.opBoolean","MERGE",FACE,{"derivedFrom":[makeQuery(id+"F5.boolean.opBoolean","MERGE",FACE,{"derivedFrom":[makeQuery(id+"F3.boolean.opBoolean","MERGE",FACE,{"derivedFrom":[makeQuery(id+"F1.opExtrude","SWEPT_FACE",FACE,{"disambiguationData":[OSD([sQuery(id+"F0.wireOp",EDGE,"E1"),sQuery(id+"F0.wireOp",EDGE,"E6"),sQuery(id+"F0.wireOp",EDGE,"E11"),sQuery(id+"F0.wireOp",EDGE,"E15")])]}),makeQuery(id+"F3.opExtrude","SWEPT_FACE",FACE,{"disambiguationData":[OSD([sQuery(id+"F2.wireOp",EDGE,"E26")])]}),makeQuery(id+"F3.opExtrude","SWEPT_FACE",FACE,{"disambiguationData":[OSD([sQuery(id+"F2.wireOp",EDGE,"E32"),sQuery(id+"F2.wireOp",EDGE,"E36")])]})]}),makeQuery(id+"F5.opExtrude","SWEPT_FACE",FACE,{"disambiguationData":[OSD([sQuery(id+"F4.wireOp",EDGE,"E50"),sQuery(id+"F4.wireOp",EDGE,"E54")])]})]}),makeQuery(id+"F8.opExtrude","SWEPT_FACE",FACE,{"disambiguationData":[OSD([sQuery(id+"F0.wireOp",EDGE,"E16")])]})]})]});
            fillet(context, id + "F14", {"entities" : qUnion([Q0, Q1, Q2, Q3, Q4, Q5]), "radius" : 5 * mm, "tangentPropagation" : true, "allowEdgeOverflow" : false});
        }
        {
            var Q0;
            Q0=makeQuery(id+"F7.boolean.opBoolean","MERGE",EDGE,{"derivedFrom":[makeQuery(id+"F5.boolean.opBoolean","MERGE",EDGE,{"derivedFrom":[makeQuery(id+"F3.boolean.opBoolean","MERGE",EDGE,{"derivedFrom":[makeQuery(id+"F1.opExtrude","SWEPT_EDGE",EDGE,{"disambiguationData":[OSD([sQuery(id+"F0.wireOp",EDGE,"E13"),sQuery(id+"F0.wireOp",EDGE,"E14")])]}),makeQuery(id+"F3.opExtrude","SWEPT_EDGE",EDGE,{"disambiguationData":[OSD([sQuery(id+"F2.wireOp",EDGE,"E34"),sQuery(id+"F2.wireOp",EDGE,"E35")])]})]}),makeQuery(id+"F5.opExtrude","SWEPT_EDGE",EDGE,{"disambiguationData":[OSD([sQuery(id+"F4.wireOp",EDGE,"E52"),sQuery(id+"F4.wireOp",EDGE,"E53")])]})]}),makeQuery(id+"F7.opExtrude","SWEPT_EDGE",EDGE,{"disambiguationData":[OSD([sQuery(id+"F6.wireOp",EDGE,"E70"),sQuery(id+"F6.wireOp",EDGE,"E71")])]})]});
            fillet(context, id + "F15", {"entities" : qUnion([Q0]), "radius" : 5 * mm, "tangentPropagation" : true, "allowEdgeOverflow" : false});
        }
        {
            var Q0;
            Q0=makeQuery(id+"F13.opFillet","BLEND_EDGE",EDGE,{"blendedFrom":[makeQuery(id+"F3.opExtrude","CAP_EDGE",EDGE,{"disambiguationData":[OSD([sQuery(id+"F2.wireOp",EDGE,"E28")])],"isStart":false}),makeQuery(id+"F3.opExtrude","SWEPT_FACE",FACE,{"disambiguationData":[OSD([sQuery(id+"F2.wireOp",EDGE,"E23")])]})],"blendedInto":[makeQuery(id+"F3.opExtrude","SWEPT_FACE",FACE,{"disambiguationData":[OSD([sQuery(id+"F2.wireOp",EDGE,"E23")])]})]});
            var Q1;
            Q1=makeQuery(id+"F13.opFillet","BLEND_EDGE",EDGE,{"blendedFrom":[makeQuery(id+"F3.opExtrude","CAP_EDGE",EDGE,{"disambiguationData":[OSD([sQuery(id+"F2.wireOp",EDGE,"E27")])],"isStart":false}),makeQuery(id+"F3.opExtrude","SWEPT_FACE",FACE,{"disambiguationData":[OSD([sQuery(id+"F2.wireOp",EDGE,"E22")])]})],"blendedInto":[makeQuery(id+"F3.opExtrude","SWEPT_FACE",FACE,{"disambiguationData":[OSD([sQuery(id+"F2.wireOp",EDGE,"E22")])]})]});
            var Q2;
            Q2=makeQuery(id+"F13.opFillet","BLEND_EDGE",EDGE,{"blendedFrom":[makeQuery(id+"F7.opExtrude","CAP_EDGE",EDGE,{"disambiguationData":[OSD([sQuery(id+"F6.wireOp",EDGE,"E71")])],"isStart":false}),makeQuery(id+"F7.opExtrude","SWEPT_FACE",FACE,{"disambiguationData":[OSD([sQuery(id+"F6.wireOp",EDGE,"E67")])]})],"blendedInto":[makeQuery(id+"F7.opExtrude","SWEPT_FACE",FACE,{"disambiguationData":[OSD([sQuery(id+"F6.wireOp",EDGE,"E67")])]})]});
            var Q3;
            Q3=makeQuery(id+"F13.opFillet","BLEND_EDGE",EDGE,{"blendedFrom":[makeQuery(id+"F7.opExtrude","CAP_EDGE",EDGE,{"disambiguationData":[OSD([sQuery(id+"F6.wireOp",EDGE,"E70")])],"isStart":false}),makeQuery(id+"F7.opExtrude","SWEPT_FACE",FACE,{"disambiguationData":[OSD([sQuery(id+"F6.wireOp",EDGE,"E73")])]})],"blendedInto":[makeQuery(id+"F7.opExtrude","SWEPT_FACE",FACE,{"disambiguationData":[OSD([sQuery(id+"F6.wireOp",EDGE,"E73")])]})]});
            var Q4;
            Q4=makeQuery(id+"F5.opExtrude","CAP_EDGE",EDGE,{"disambiguationData":[OSD([sQuery(id+"F4.wireOp",EDGE,"E38")])],"isStart":false});
            fillet(context, id + "F16", {"entities" : qUnion([Q0, Q1, Q2, Q3, Q4]), "radius" : 1.3 * mm, "tangentPropagation" : true, "allowEdgeOverflow" : false});
        }
    });
